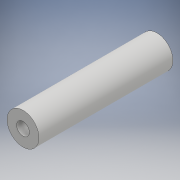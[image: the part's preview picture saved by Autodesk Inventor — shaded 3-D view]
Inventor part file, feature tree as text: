
AUTODESK INVENTOR PART (.ipt)
format: ipt  version: 2018 (Build 220112000, 112)  size: 95,232 bytes
history: native  units: mm
features: extrude x1, sketch x1
ambient origin geometry x8: Origin, YZ Plane, XZ Plane, XY Plane, X Axis, Y Axis, Z Axis, Center Point
bodies: Solid1 (feature_tree)
feature tree (2):
  extrude  "Extrusion1"  Depth=42.0mm
  sketch  "Sketch1"  dims[d0=10.0mm d1=4.0mm d2=42.0mm d3=0.0mm]
